# Revit family: Lighting-Recessed-Luminii-Glint-Hero-Wood_Grille
name_source: partatom
category: Lighting Fixtures
units: mm (PartAtom-declared; Revit-internal decimal feet)

## family parameters
Cut with Voids When Loaded = No
Host = Face
Light Source = No
OmniClass Number = 23.80.70.11.14.11
OmniClass Title = Downlights
Part Type = Normal
Room Calculation Point = No
Round Connector Dimension = Use Diameter
Shared = No

## types (2) — shared parameters
Apparent Load = 0 VA
Assembly Code = D5020200
Bracket Finish = Aluminum - Luminii - White
Default Elevation = 48.0000"
Description = Lightshift Adjustable Luminaire
Fixture Height = 3.0000"
Host Width = 13.7520"
Housing Finish = Aluminum - Luminii - White
Keynote = 16510
Lens Finish = Acrylic - Luminii - Frosted
Manufacturer = Luminii
Model = Hero Wood Grille
Trim Finish = Aluminum - Luminii - Black
URL = https://www.luminii.com
Voltage = 120 V
Wattage = 23 W
Width = 1.7520"

## type names (no varying parameters)
- Recessed
- Wood Grille

## geometry (parser evidence)
native form markers: Sweep x39
no freeform markers — native parametric forms only
